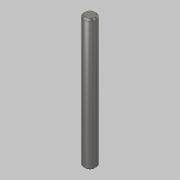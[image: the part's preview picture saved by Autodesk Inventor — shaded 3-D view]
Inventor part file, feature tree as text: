
AUTODESK INVENTOR PART (.ipt)
format: ipt  version: 2019.2 (Build 232265000, 265)  size: 81,920 bytes
history: native  units: mm
features: other x1, extrude x1, chamfer x1, sketch x1
ambient origin geometry x8: Origin, YZ Plane, XZ Plane, XY Plane, X Axis, Y Axis, Z Axis, Center Point
bodies: Body1 (feature_tree)
feature tree (4):
  other  "Shaft1.ipt"
  extrude  "Extrusion1"  Depth=21.5mm TaperAngle=0.0deg
  chamfer  "Fase1"  Distance=0.25mm Angle=45.0deg
  sketch  "Skizze1"  dims[d3=10.0mm d4=21.5mm d5=0.0mm d6=0.25mm d7=2.0mm d8=45.0deg]
